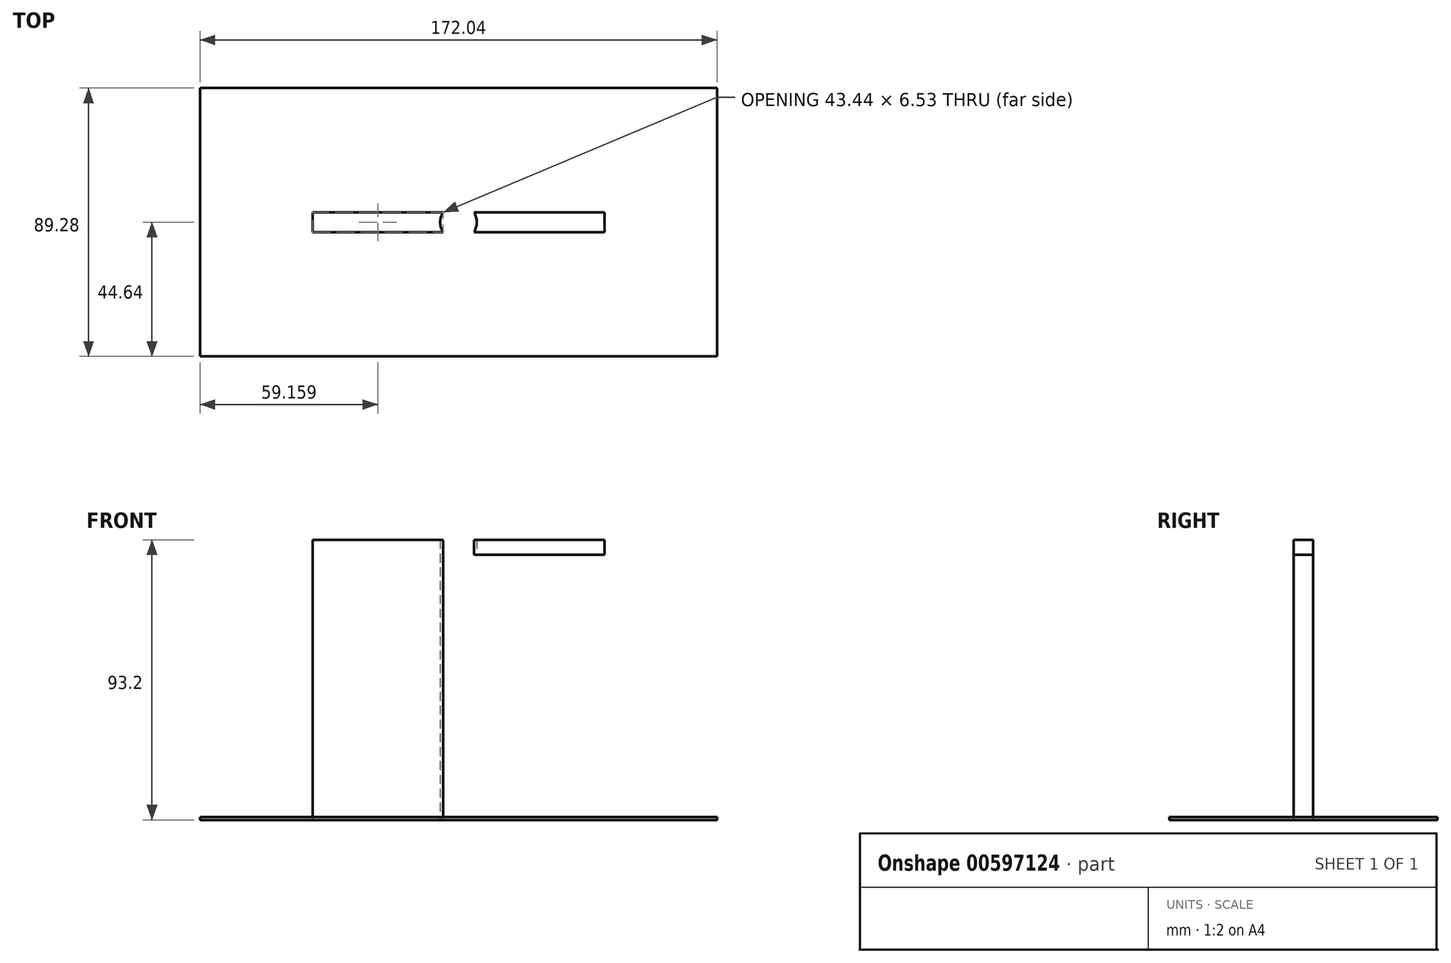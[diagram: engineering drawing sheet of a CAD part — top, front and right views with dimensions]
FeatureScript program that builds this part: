
annotation { "Feature Type Name" : "Feature", "Feature Type Description" : "" }
export const myFeature = defineFeature(function(context is Context, id is Id, definition is map)
    precondition{}
    {
        {
            var Q0;
            Q0=qCreatedBy(makeId("Top.planeOp"),FACE);
            var sketch = newSketch(context, id + "F0", { "sketchPlane" : qUnion([Q0])});
            skLineSegment(sketch, "E0.bottom", {"start": v(48.58, -3.26) * mm, "end": v(-48.58, -3.26) * mm});
            skLineSegment(sketch, "E0.top", {"start": v(48.58, 3.26) * mm, "end": v(-48.58, 3.26) * mm});
            skLineSegment(sketch, "E0.left", {"start": v(48.58, -3.26) * mm, "end": v(48.58, 3.26) * mm});
            skLineSegment(sketch, "E0.right", {"start": v(-48.58, -3.26) * mm, "end": v(-48.58, 3.26) * mm});
            skPoint(sketch, "E0.middle", {"position": v(0, 0) * mm});
            skCircle(sketch, "E1", {"center": v(0, 0) * mm, "radius": 6.1 * mm});
            skSolve(sketch);
        }
        {
            var Q0;
            {var subQ0=sQuery(id+"F0.wireOp",EDGE,"E0.right");Q0=makeQuery(id+"F0.imprint","IMPRINT",FACE,{"disambiguationData":[TD([[makeQuery(id+"F0.imprint","IMPRINT",EDGE,{"derivedFrom":subQ0}),-1.0]])]});}
            var Q1;
            {var subQ0=sQuery(id+"F0.wireOp",EDGE,"E1");var subQ1=sQuery(id+"F0.wireOp",EDGE,"E0.bottom");var subQ2=makeQuery(id+"F0.imprint","INTERSECT",VERTEX,{"disambiguationData":[OD(0.0)],"derivedFrom":[subQ1,subQ0]});Q1=makeQuery(id+"F0.imprint","IMPRINT",FACE,{"disambiguationData":[TD([[makeQuery(id+"F0.imprint","IMPRINT",EDGE,{"disambiguationData":[TD([[subQ2,-1.0]])],"derivedFrom":subQ1}),-1.0]])]});}
            var Q2;
            {var subQ0=sQuery(id+"F0.wireOp",EDGE,"E0.left");Q2=makeQuery(id+"F0.imprint","IMPRINT",FACE,{"disambiguationData":[TD([[makeQuery(id+"F0.imprint","IMPRINT",EDGE,{"derivedFrom":subQ0}),1.0]])]});}
            extrude(context, id + "F1", {"entities" : qUnion([Q0, Q1, Q2]), "depth" : 5 * mm, "offsetDistance" : 25 * mm});
        }
        {
            var Q0;
            {var subQ0=sQuery(id+"F0.wireOp",EDGE,"E1");var subQ1=sQuery(id+"F0.wireOp",EDGE,"E0.bottom");var subQ2=makeQuery(id+"F0.imprint","INTERSECT",VERTEX,{"disambiguationData":[OD(0.0)],"derivedFrom":[subQ1,subQ0]});Q0=makeQuery(id+"F0.imprint","IMPRINT",FACE,{"disambiguationData":[TD([[makeQuery(id+"F0.imprint","IMPRINT",EDGE,{"disambiguationData":[TD([[subQ2,-1.0]])],"derivedFrom":subQ1}),1.0]])]});}
            var Q1;
            {var subQ0=sQuery(id+"F0.wireOp",EDGE,"E1");var subQ1=sQuery(id+"F0.wireOp",EDGE,"E0.top");var subQ2=makeQuery(id+"F0.imprint","INTERSECT",VERTEX,{"disambiguationData":[OD(0.0)],"derivedFrom":[subQ1,subQ0]});Q1=makeQuery(id+"F0.imprint","IMPRINT",FACE,{"disambiguationData":[TD([[makeQuery(id+"F0.imprint","IMPRINT",EDGE,{"disambiguationData":[TD([[subQ2,-1.0]])],"derivedFrom":subQ1}),-1.0]])]});}
            var Q2;
            {var subQ0=sQuery(id+"F0.wireOp",EDGE,"E1");var subQ1=sQuery(id+"F0.wireOp",EDGE,"E0.bottom");var subQ2=makeQuery(id+"F0.imprint","INTERSECT",VERTEX,{"disambiguationData":[OD(0.0)],"derivedFrom":[subQ1,subQ0]});Q2=makeQuery(id+"F0.imprint","IMPRINT",FACE,{"disambiguationData":[TD([[makeQuery(id+"F0.imprint","IMPRINT",EDGE,{"disambiguationData":[TD([[subQ2,-1.0]])],"derivedFrom":subQ1}),-1.0]])]});}
            extrude(context, id + "F2", {"entities" : qUnion([Q0, Q1, Q2]), "operationType" : NewBodyOperationType.ADD, "oppositeDirection" : true, "depth" : 87.2 * mm, "offsetDistance" : 25 * mm});
        }
        {
            var Q0;
            Q0=makeQuery(id+"F2.opExtrude","CAP_FACE",FACE,{"disambiguationData":[OSD([sQuery(id+"F0.wireOp",EDGE,"E1")])],"isStart":false});
            var sketch = newSketch(context, id + "F3", { "sketchPlane" : qUnion([Q0])});
            skLineSegment(sketch, "E2.bottom", {"start": v(86.02, -44.64) * mm, "end": v(-86.02, -44.64) * mm});
            skLineSegment(sketch, "E2.top", {"start": v(86.02, 44.64) * mm, "end": v(-86.02, 44.64) * mm});
            skLineSegment(sketch, "E2.left", {"start": v(86.02, -44.64) * mm, "end": v(86.02, 44.64) * mm});
            skLineSegment(sketch, "E2.right", {"start": v(-86.02, -44.64) * mm, "end": v(-86.02, 44.64) * mm});
            skPoint(sketch, "E2.middle", {"position": v(0, 0) * mm});
            skSolve(sketch);
        }
        {
            var Q0;
            Q0=makeQuery(id+"F3.imprint","IMPRINT",FACE,{"disambiguationData":[TD([[makeQuery(id+"F3.imprint","IMPRINT",EDGE,{"derivedFrom":sQuery(id+"F3.wireOp",EDGE,"E2.bottom")}),-1.0]])]});
            extrude(context, id + "F4", {"entities" : qUnion([Q0]), "depth" : 1 * mm, "offsetDistance" : 25 * mm});
        }
    });
